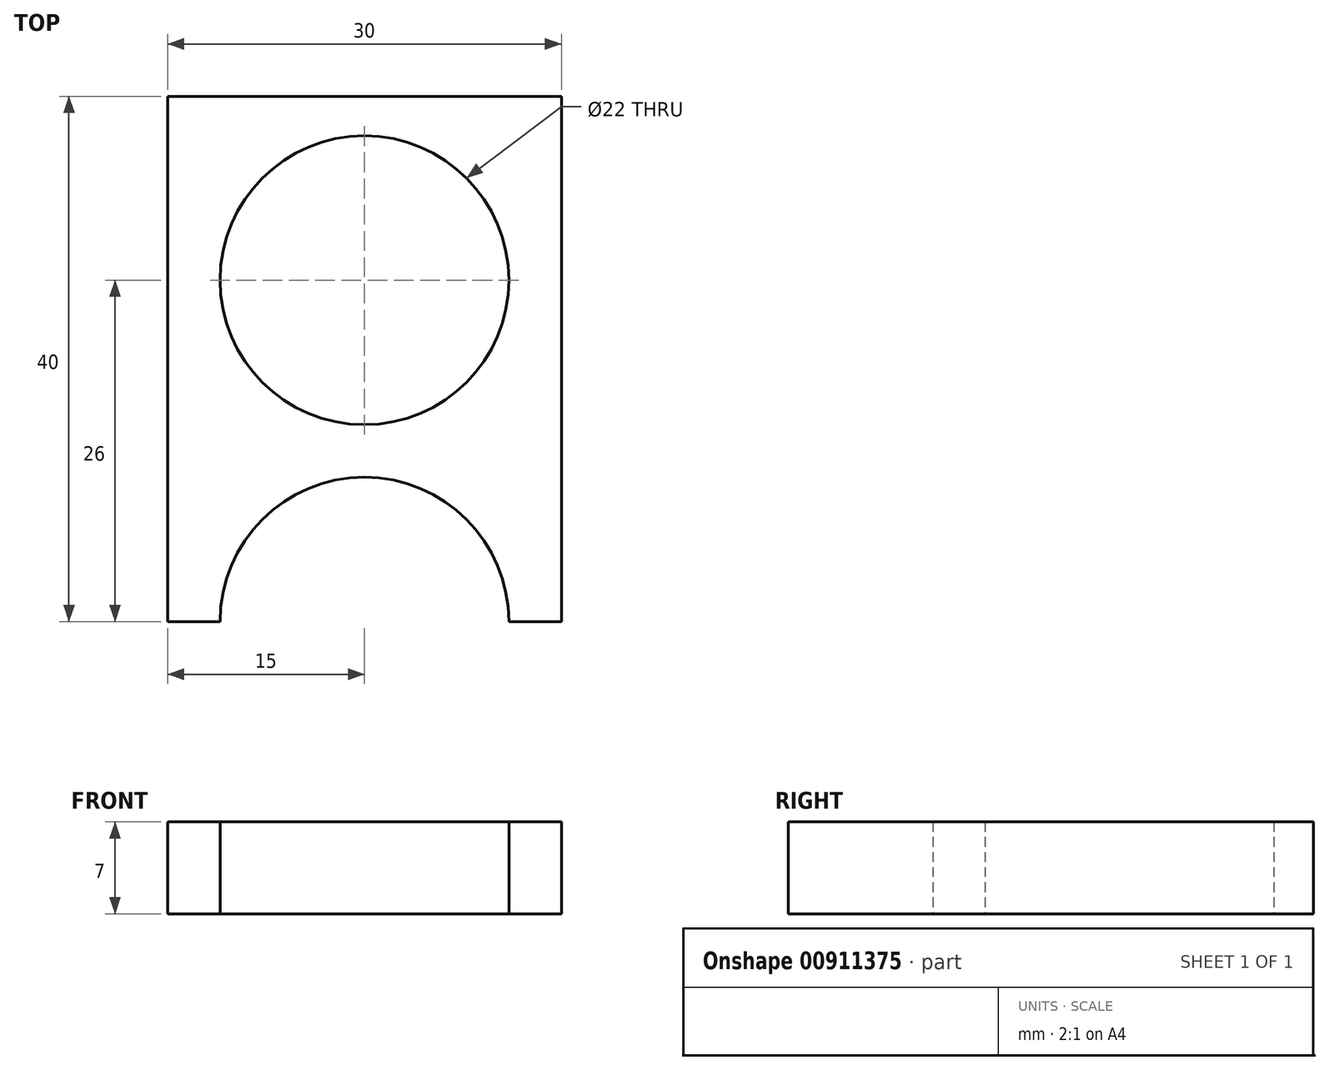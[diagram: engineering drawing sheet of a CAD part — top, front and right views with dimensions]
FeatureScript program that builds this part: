
annotation { "Feature Type Name" : "Feature", "Feature Type Description" : "" }
export const myFeature = defineFeature(function(context is Context, id is Id, definition is map)
    precondition{}
    {
        {
            var Q0;
            Q0=qCreatedBy(makeId("Top.planeOp"),FACE);
            var sketch = newSketch(context, id + "F0", { "sketchPlane" : qUnion([Q0])});
            skCircle(sketch, "E0", {"center": v(0, 0) * mm, "radius": 11 * mm});
            skLineSegment(sketch, "E1.bottom", {"start": v(0, 0) * mm, "end": v(15, 0) * mm});
            skLineSegment(sketch, "E1.top", {"start": v(0, 40) * mm, "end": v(15, 40) * mm});
            skLineSegment(sketch, "E1.left", {"start": v(0, 0) * mm, "end": v(0, 40) * mm});
            skLineSegment(sketch, "E1.right", {"start": v(15, 0) * mm, "end": v(15, 40) * mm});
            skLineSegment(sketch, "E2.bottom", {"start": v(0, 0) * mm, "end": v(-15, 0) * mm});
            skLineSegment(sketch, "E2.top", {"start": v(0, 40) * mm, "end": v(-15, 40) * mm});
            skLineSegment(sketch, "E2.right", {"start": v(-15, 0) * mm, "end": v(-15, 40) * mm});
            skLineSegment(sketch, "E3", {"start": v(0, 40) * mm, "end": v(0, 26) * mm});
            skCircle(sketch, "E4", {"center": v(0, 26) * mm, "radius": 11 * mm});
            skSolve(sketch);
        }
        {
            var Q0;
            {var subQ9=sQuery(id+"F0.wireOp",EDGE,"E1.top");Q0=makeQuery(id+"F0.imprint","IMPRINT",FACE,{"disambiguationData":[TD([[makeQuery(id+"F0.imprint","IMPRINT",EDGE,{"derivedFrom":subQ9}),-1.0]])]});}
            var Q1;
            {var subQ0=sQuery(id+"F0.wireOp",EDGE,"E2.top");Q1=makeQuery(id+"F0.imprint","IMPRINT",FACE,{"disambiguationData":[TD([[makeQuery(id+"F0.imprint","IMPRINT",EDGE,{"derivedFrom":subQ0}),1.0]])]});}
            extrude(context, id + "F1", {"entities" : qUnion([Q0, Q1]), "depth" : 7 * mm, "offsetDistance" : 25 * mm});
        }
    });
